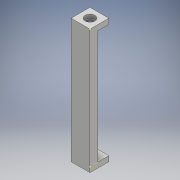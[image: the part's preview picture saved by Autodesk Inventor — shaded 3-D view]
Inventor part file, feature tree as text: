
AUTODESK INVENTOR PART (.ipt)
format: ipt  version: 2018 (Build 220112000, 112)  size: 154,112 bytes
history: native  units: mm
features: sketch x9, extrude x6, fillet x1
ambient origin geometry x8: Origin, YZ Plane, XZ Plane, XY Plane, X Axis, Y Axis, Z Axis, Center Point
bodies: Solid1 (feature_tree)
feature tree (16):
  extrude  "Extrusion1"  Depth=165.0mm
  extrude  "Extrusion2"  Depth=7.0mm
  sketch  "Sketch3"  dims[d5=7.0mm d6=22.0mm d7=0.0mm]
  extrude  "Extrusion3"  Depth=22.0mm TaperAngle=0.0deg
  extrude  "Extrusion4"  Depth=5.0mm TaperAngle=0.0deg
  extrude  "Extrusion5"  Depth=10.0mm
  sketch  "Sketch7"  dims[d18=7.5mm d19=0.0mm]
  sketch  "Sketch8"  dims[d20=2.0mm]
  extrude  "Extrusion6"  Depth=5.0mm
  fillet  "Fillet1"  Radius=5.0mm
  sketch  "Sketch1"  dims[d0=25.0mm d1=165.0mm]
  sketch  "Sketch2"  dims[d2=3.0mm d3=0.0mm d4=7.0mm]
  sketch  "Sketch4"  dims[d8=13.0mm d9=5.0mm d10=0.0mm]
  sketch  "Sketch5"  dims[d11=5.0mm d12=0.0mm d13=10.0mm]
  sketch  "Sketch6"  dims[d14=165.0mm d15=0.0mm d16=5.0mm d17=5.0mm]
  sketch  "Sketch9"
